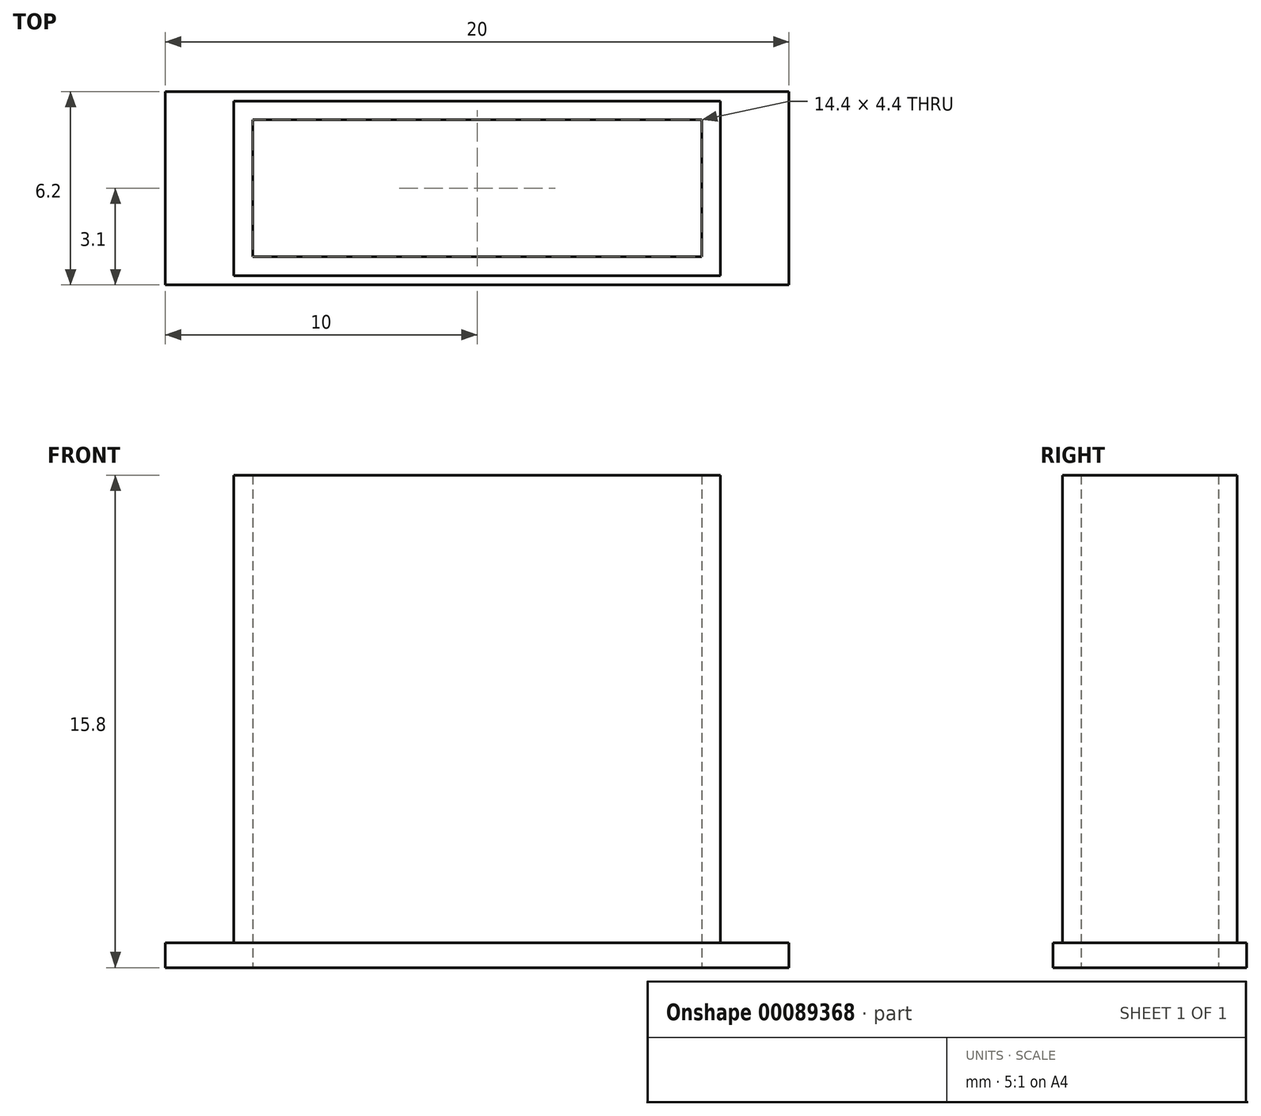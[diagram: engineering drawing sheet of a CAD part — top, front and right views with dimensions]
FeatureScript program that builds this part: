
annotation { "Feature Type Name" : "Feature", "Feature Type Description" : "" }
export const myFeature = defineFeature(function(context is Context, id is Id, definition is map)
    precondition{}
    {
        {
            var Q0;
            Q0=qCreatedBy(makeId("Top.planeOp"),FACE);
            var sketch = newSketch(context, id + "F0", { "sketchPlane" : qUnion([Q0])});
            skLineSegment(sketch, "E0.bottom", {"start": v(10, 3.1) * mm, "end": v(-10, 3.1) * mm});
            skLineSegment(sketch, "E0.top", {"start": v(10, -3.1) * mm, "end": v(-10, -3.1) * mm});
            skLineSegment(sketch, "E0.left", {"start": v(10, 3.1) * mm, "end": v(10, -3.1) * mm});
            skLineSegment(sketch, "E0.right", {"start": v(-10, 3.1) * mm, "end": v(-10, -3.1) * mm});
            skPoint(sketch, "E0.middle", {"position": v(0, 0) * mm});
            skLineSegment(sketch, "E1.bottom", {"start": v(7.2, 2.2) * mm, "end": v(-7.2, 2.2) * mm});
            skLineSegment(sketch, "E1.top", {"start": v(7.2, -2.2) * mm, "end": v(-7.2, -2.2) * mm});
            skLineSegment(sketch, "E1.left", {"start": v(7.2, 2.2) * mm, "end": v(7.2, -2.2) * mm});
            skLineSegment(sketch, "E1.right", {"start": v(-7.2, 2.2) * mm, "end": v(-7.2, -2.2) * mm});
            skSolve(sketch);
        }
        {
            var Q0;
            Q0 = qSketchRegion(id + "F0", true);
            extrude(context, id + "F1", {"entities" : qUnion([Q0]), "depth" : 0.8 * mm});
        }
        {
            var Q0;
            Q0=makeQuery(id+"F1.opExtrude","CAP_FACE",FACE,{"disambiguationData":[OSD([sQuery(id+"F0.wireOp",EDGE,"E0.bottom"),sQuery(id+"F0.wireOp",EDGE,"E0.top"),sQuery(id+"F0.wireOp",EDGE,"E0.left"),sQuery(id+"F0.wireOp",EDGE,"E0.right"),sQuery(id+"F0.wireOp",EDGE,"E1.bottom"),sQuery(id+"F0.wireOp",EDGE,"E1.top"),sQuery(id+"F0.wireOp",EDGE,"E1.left"),sQuery(id+"F0.wireOp",EDGE,"E1.right")])],"isStart":false});
            var sketch = newSketch(context, id + "F2", { "sketchPlane" : qUnion([Q0])});
            skLineSegment(sketch, "E2.bottom", {"start": v(7.2, 2.2) * mm, "end": v(-7.2, 2.2) * mm});
            skLineSegment(sketch, "E2.top", {"start": v(7.2, -2.2) * mm, "end": v(-7.2, -2.2) * mm});
            skLineSegment(sketch, "E2.left", {"start": v(7.2, 2.2) * mm, "end": v(7.2, -2.2) * mm});
            skLineSegment(sketch, "E2.right", {"start": v(-7.2, 2.2) * mm, "end": v(-7.2, -2.2) * mm});
            skPoint(sketch, "E2.middle", {"position": v(0, 0) * mm});
            skLineSegment(sketch, "E3.bottom", {"start": v(7.8, 2.8) * mm, "end": v(-7.8, 2.8) * mm});
            skLineSegment(sketch, "E3.top", {"start": v(7.8, -2.8) * mm, "end": v(-7.8, -2.8) * mm});
            skLineSegment(sketch, "E3.left", {"start": v(7.8, 2.8) * mm, "end": v(7.8, -2.8) * mm});
            skLineSegment(sketch, "E3.right", {"start": v(-7.8, 2.8) * mm, "end": v(-7.8, -2.8) * mm});
            skSolve(sketch);
        }
        {
            var Q0;
            Q0 = qSketchRegion(id + "F2", true);
            extrude(context, id + "F3", {"entities" : qUnion([Q0]), "operationType" : NewBodyOperationType.ADD, "depth" : 15 * mm});
        }
    });
